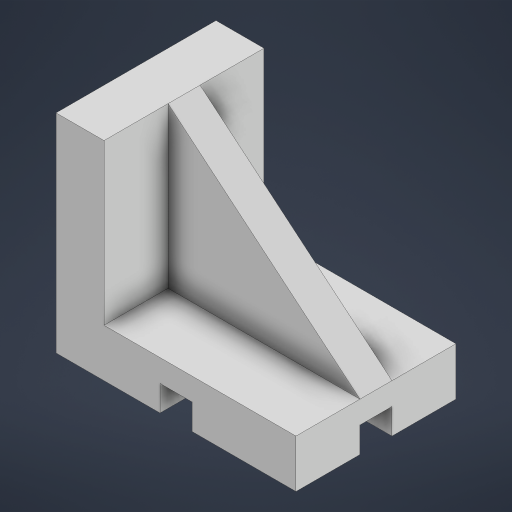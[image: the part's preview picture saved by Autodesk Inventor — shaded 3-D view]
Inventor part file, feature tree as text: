
AUTODESK INVENTOR PART (.ipt)
format: ipt  version: 2023 (Build 270158000, 158)  size: 211,456 bytes
history: native  units: mm
features: sketch x4, extrude x2, other x1
ambient origin geometry x8: Origin, YZ Plane, XZ Plane, XY Plane, X Axis, Y Axis, Z Axis, Center Point
bodies: Body1 (feature_tree)
feature tree (7):
  sketch  "Szkic6"
  extrude  "Wyciągnięcie proste3"  Depth=65.0mm
  other  "Żebro2"
  extrude  "Wyciągnięcie proste4"  Depth=75.0mm
  sketch  "Szkic7"
  sketch  "Szkic8"
  sketch  "Szkic9"
